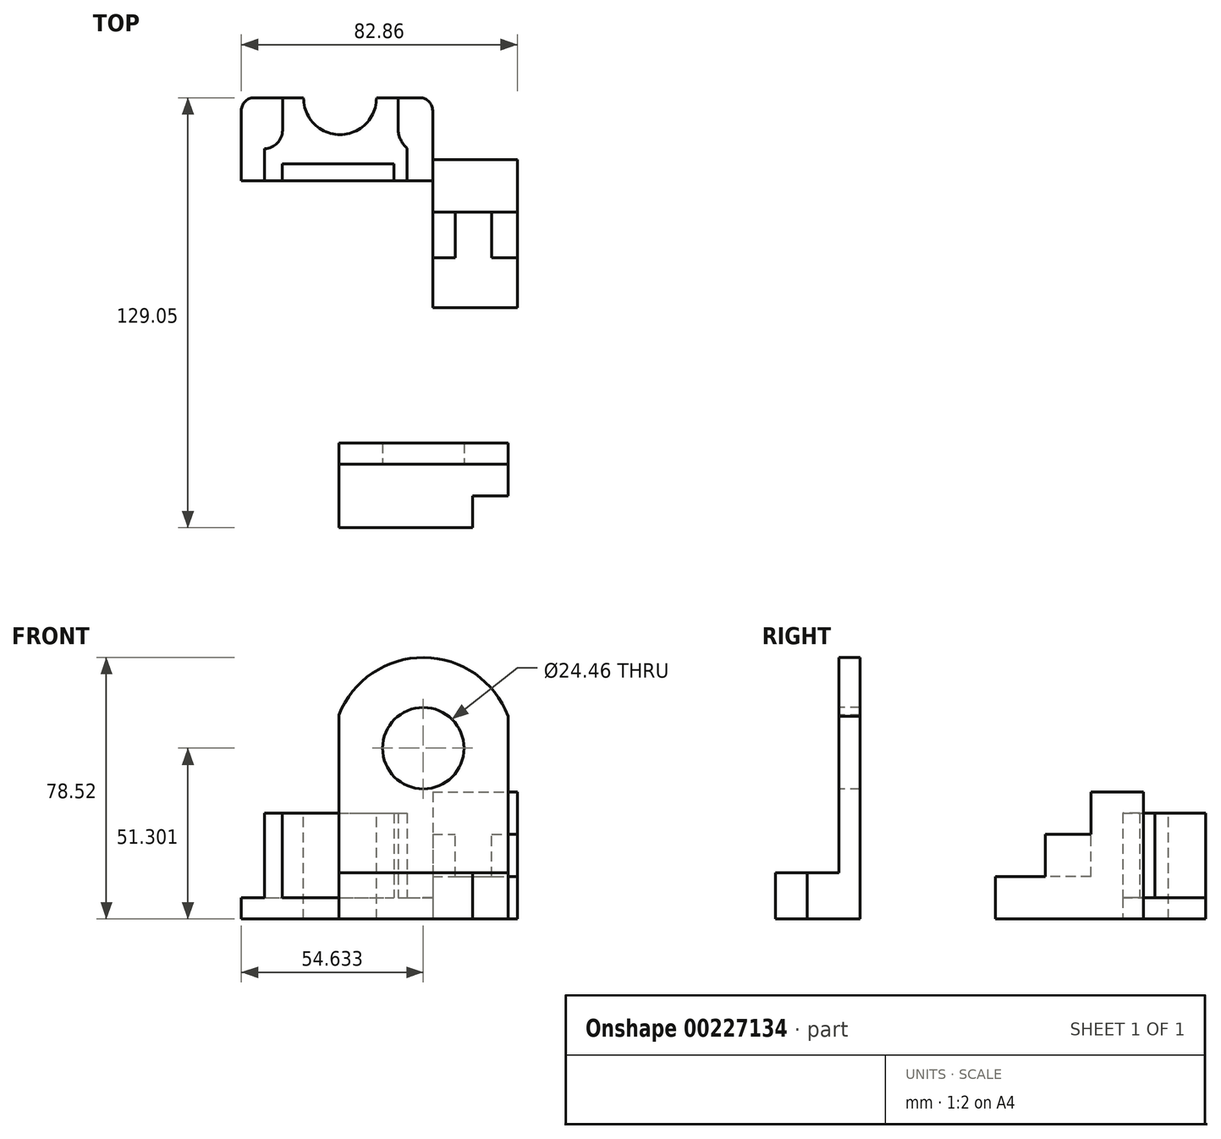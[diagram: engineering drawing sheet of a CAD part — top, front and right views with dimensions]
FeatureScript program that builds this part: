
annotation { "Feature Type Name" : "Feature", "Feature Type Description" : "" }
export const myFeature = defineFeature(function(context is Context, id is Id, definition is map)
    precondition{}
    {
        {
            var Q0;
            Q0=qCreatedBy(makeId("Top.planeOp"),FACE);
            var sketch = newSketch(context, id + "F0", { "sketchPlane" : qUnion([Q0])});
            skLineSegment(sketch, "E0.bottom", {"start": v(0, 0) * mm, "end": v(25.4, 0) * mm});
            skLineSegment(sketch, "E0.top", {"start": v(0, 44.45) * mm, "end": v(25.4, 44.45) * mm});
            skLineSegment(sketch, "E0.left", {"start": v(0, 0) * mm, "end": v(0, 44.45) * mm});
            skLineSegment(sketch, "E0.right", {"start": v(25.4, 0) * mm, "end": v(25.4, 44.45) * mm});
            skSolve(sketch);
        }
        {
            var Q0;
            Q0=makeQuery(id+"F0.imprint","IMPRINT",FACE,{"disambiguationData":[TD([[makeQuery(id+"F0.imprint","IMPRINT",EDGE,{"derivedFrom":sQuery(id+"F0.wireOp",EDGE,"E0.bottom")}),1.0]])]});
            extrude(context, id + "F1", {"entities" : qUnion([Q0]), "depth" : 12.7 * mm});
        }
        {
            var Q0;
            Q0=makeQuery(id+"F1.opExtrude","CAP_FACE",FACE,{"disambiguationData":[OSD([sQuery(id+"F0.wireOp",EDGE,"E0.bottom"),sQuery(id+"F0.wireOp",EDGE,"E0.top"),sQuery(id+"F0.wireOp",EDGE,"E0.left"),sQuery(id+"F0.wireOp",EDGE,"E0.right")])],"isStart":false});
            var sketch = newSketch(context, id + "F2", { "sketchPlane" : qUnion([Q0])});
            skLineSegment(sketch, "E1.bottom", {"start": v(0, 44.45) * mm, "end": v(25.4, 44.45) * mm});
            skLineSegment(sketch, "E1.top", {"start": v(0, 14.99) * mm, "end": v(25.4, 14.99) * mm});
            skLineSegment(sketch, "E1.left", {"start": v(0, 44.45) * mm, "end": v(0, 14.99) * mm});
            skLineSegment(sketch, "E1.right", {"start": v(25.4, 44.45) * mm, "end": v(25.4, 14.99) * mm});
            skSolve(sketch);
        }
        {
            var Q0;
            Q0 = qSketchRegion(id + "F2", true);
            extrude(context, id + "F3", {"entities" : qUnion([Q0]), "operationType" : NewBodyOperationType.ADD, "depth" : 12.7 * mm});
        }
        {
            var Q0;
            Q0=makeQuery(id+"F3.opExtrude","CAP_FACE",FACE,{"disambiguationData":[OSD([sQuery(id+"F2.wireOp",EDGE,"E1.bottom"),sQuery(id+"F2.wireOp",EDGE,"E1.top"),sQuery(id+"F2.wireOp",EDGE,"E1.left"),sQuery(id+"F2.wireOp",EDGE,"E1.right")])],"isStart":false});
            var sketch = newSketch(context, id + "F4", { "sketchPlane" : qUnion([Q0])});
            skLineSegment(sketch, "E2.bottom", {"start": v(6.74, 28.65) * mm, "end": v(17.73, 28.65) * mm});
            skLineSegment(sketch, "E2.top", {"start": v(6.74, 14.99) * mm, "end": v(17.73, 14.99) * mm});
            skLineSegment(sketch, "E2.left", {"start": v(6.74, 28.65) * mm, "end": v(6.74, 14.99) * mm});
            skLineSegment(sketch, "E2.right", {"start": v(17.73, 28.65) * mm, "end": v(17.73, 14.99) * mm});
            skSolve(sketch);
        }
        {
            var Q0;
            Q0 = qSketchRegion(id + "F4", true);
            extrude(context, id + "F5", {"entities" : qUnion([Q0]), "operationType" : NewBodyOperationType.REMOVE, "oppositeDirection" : true, "depth" : 12.7 * mm});
        }
        {
            var Q0;
            Q0=makeQuery(id+"F3.opExtrude","CAP_FACE",FACE,{"disambiguationData":[OSD([sQuery(id+"F2.wireOp",EDGE,"E1.bottom"),sQuery(id+"F2.wireOp",EDGE,"E1.top"),sQuery(id+"F2.wireOp",EDGE,"E1.left"),sQuery(id+"F2.wireOp",EDGE,"E1.right")])],"isStart":false});
            var sketch = newSketch(context, id + "F6", { "sketchPlane" : qUnion([Q0])});
            skLineSegment(sketch, "E3.bottom", {"start": v(0, 44.45) * mm, "end": v(25.4, 44.45) * mm});
            skLineSegment(sketch, "E3.top", {"start": v(0, 28.65) * mm, "end": v(25.4, 28.65) * mm});
            skLineSegment(sketch, "E3.left", {"start": v(0, 44.45) * mm, "end": v(0, 28.65) * mm});
            skLineSegment(sketch, "E3.right", {"start": v(25.4, 44.45) * mm, "end": v(25.4, 28.65) * mm});
            skSolve(sketch);
        }
        {
            var Q0;
            Q0=makeQuery(id+"F6.imprint","IMPRINT",FACE,{"disambiguationData":[TD([[makeQuery(id+"F6.imprint","IMPRINT",EDGE,{"derivedFrom":sQuery(id+"F6.wireOp",EDGE,"E3.bottom")}),-1.0]])]});
            extrude(context, id + "F7", {"entities" : qUnion([Q0]), "operationType" : NewBodyOperationType.ADD, "depth" : 12.7 * mm});
        }
        {
            var Q0;
            Q0=qCreatedBy(makeId("Top.planeOp"),FACE);
            var sketch = newSketch(context, id + "F8", { "sketchPlane" : qUnion([Q0])});
            skLineSegment(sketch, "E4.bottom", {"start": v(-28.17, -66.03) * mm, "end": v(22.63, -66.03) * mm});
            skLineSegment(sketch, "E4.top", {"start": v(-28.17, -40.63) * mm, "end": v(22.63, -40.63) * mm});
            skLineSegment(sketch, "E4.left", {"start": v(-28.17, -66.03) * mm, "end": v(-28.17, -40.63) * mm});
            skLineSegment(sketch, "E4.right", {"start": v(22.63, -66.03) * mm, "end": v(22.63, -40.63) * mm});
            skSolve(sketch);
        }
        {
            var Q0;
            Q0=makeQuery(id+"F8.imprint","IMPRINT",FACE,{"disambiguationData":[TD([[makeQuery(id+"F8.imprint","IMPRINT",EDGE,{"derivedFrom":sQuery(id+"F8.wireOp",EDGE,"E4.bottom")}),1.0]])]});
            extrude(context, id + "F9", {"entities" : qUnion([Q0]), "depth" : 101.6 * mm});
        }
        {
            var Q0;
            Q0=makeQuery(id+"F9.opExtrude","SWEPT_FACE",FACE,{"disambiguationData":[OSD([sQuery(id+"F8.wireOp",EDGE,"E4.bottom")])]});
            var sketch = newSketch(context, id + "F10", { "sketchPlane" : qUnion([Q0])});
            skArc(sketch, "E5", {"start": v(22.63, 60.92) * mm, "mid": v(-2.66, 78.52) * mm, "end": v(-28.17, 61.23) * mm});
            skSolve(sketch);
        }
        {
            var Q0;
            {var subQ0=sQuery(id+"F10.wireOp",EDGE,"E5");Q0=makeQuery(id+"F10.imprint","IMPRINT",FACE,{"disambiguationData":[TD([[makeQuery(id+"F10.imprint","IMPRINT",EDGE,{"derivedFrom":subQ0}),-1.0]])]});}
            extrude(context, id + "F11", {"entities" : qUnion([Q0]), "operationType" : NewBodyOperationType.REMOVE, "oppositeDirection" : true, "depth" : 25.4 * mm});
        }
        {
            var Q0;
            Q0=makeQuery(id+"F9.opExtrude","SWEPT_FACE",FACE,{"disambiguationData":[OSD([sQuery(id+"F8.wireOp",EDGE,"E4.bottom")])]});
            var sketch = newSketch(context, id + "F12", { "sketchPlane" : qUnion([Q0])});
            skCircle(sketch, "E6", {"center": v(-2.83, 51.3) * mm, "radius": 12.23 * mm});
            skSolve(sketch);
        }
        {
            var Q0;
            Q0=makeQuery(id+"F12.imprint","IMPRINT",FACE,{"disambiguationData":[TD([[makeQuery(id+"F12.imprint","IMPRINT",EDGE,{"derivedFrom":sQuery(id+"F12.wireOp",EDGE,"E6")}),1.0]])]});
            extrude(context, id + "F13", {"entities" : qUnion([Q0]), "operationType" : NewBodyOperationType.REMOVE, "oppositeDirection" : true, "depth" : 25.4 * mm});
        }
        {
            var Q0;
            Q0=makeQuery(id+"F9.opExtrude","SWEPT_FACE",FACE,{"disambiguationData":[OSD([sQuery(id+"F8.wireOp",EDGE,"E4.bottom")])]});
            var sketch = newSketch(context, id + "F14", { "sketchPlane" : qUnion([Q0])});
            skLineSegment(sketch, "E7.bottom", {"start": v(-28.17, 13.84) * mm, "end": v(22.63, 13.84) * mm});
            skLineSegment(sketch, "E7.top", {"start": v(-28.17, 0) * mm, "end": v(22.63, 0) * mm});
            skLineSegment(sketch, "E7.left", {"start": v(-28.17, 13.84) * mm, "end": v(-28.17, 0) * mm});
            skLineSegment(sketch, "E7.right", {"start": v(22.63, 13.84) * mm, "end": v(22.63, 0) * mm});
            skSolve(sketch);
        }
        {
            var Q0;
            {var subQ3=sQuery(id+"F14.wireOp",EDGE,"E7.bottom");Q0=makeQuery(id+"F14.imprint","IMPRINT",FACE,{"disambiguationData":[TD([[makeQuery(id+"F14.imprint","IMPRINT",EDGE,{"derivedFrom":subQ3}),1.0]])]});}
            extrude(context, id + "F15", {"entities" : qUnion([Q0]), "operationType" : NewBodyOperationType.REMOVE, "oppositeDirection" : true, "depth" : 19.05 * mm});
        }
        {
            var Q0;
            Q0=makeQuery(id+"F15.boolean.opBoolean","COPY",FACE,{"derivedFrom":makeQuery(id+"F15.opExtrude","SWEPT_FACE",FACE,{"disambiguationData":[OSD([sQuery(id+"F14.wireOp",EDGE,"E7.bottom")])]})});
            var sketch = newSketch(context, id + "F16", { "sketchPlane" : qUnion([Q0])});
            skLineSegment(sketch, "E8.bottom", {"start": v(22.63, -56.5) * mm, "end": v(11.96, -56.5) * mm});
            skLineSegment(sketch, "E8.top", {"start": v(22.63, -66.03) * mm, "end": v(11.96, -66.03) * mm});
            skLineSegment(sketch, "E8.left", {"start": v(22.63, -56.5) * mm, "end": v(22.63, -66.03) * mm});
            skLineSegment(sketch, "E8.right", {"start": v(11.96, -56.5) * mm, "end": v(11.96, -66.03) * mm});
            skSolve(sketch);
        }
        {
            var Q0;
            Q0=makeQuery(id+"F16.imprint","IMPRINT",FACE,{"disambiguationData":[TD([[makeQuery(id+"F16.imprint","IMPRINT",EDGE,{"derivedFrom":sQuery(id+"F16.wireOp",EDGE,"E8.bottom")}),1.0]])]});
            extrude(context, id + "F17", {"entities" : qUnion([Q0]), "operationType" : NewBodyOperationType.REMOVE, "oppositeDirection" : true, "depth" : 25.4 * mm});
        }
        {
            var Q0;
            Q0=qCreatedBy(makeId("Top.planeOp"),FACE);
            var sketch = newSketch(context, id + "F18", { "sketchPlane" : qUnion([Q0])});
            skLineSegment(sketch, "E9.bottom", {"start": v(-53.65, 63.02) * mm, "end": v(-3.81, 63.02) * mm});
            skLineSegment(sketch, "E9.top", {"start": v(-57.46, 38.14) * mm, "end": v(0, 38.14) * mm});
            skLineSegment(sketch, "E9.left", {"start": v(-57.46, 59.21) * mm, "end": v(-57.46, 38.14) * mm});
            skLineSegment(sketch, "E9.right", {"start": v(0, 59.21) * mm, "end": v(0, 38.14) * mm});
            skPoint(sketch, "E10.visualSharp", {"position": v(-57.46, 63.02) * mm});
            skArc(sketch, "E10.filletArc", {"start": v(-53.65, 63.02) * mm, "mid": v(-56.35, 61.9) * mm, "end": v(-57.46, 59.21) * mm});
            skPoint(sketch, "E11.visualSharp", {"position": v(0, 63.02) * mm});
            skArc(sketch, "E11.filletArc", {"start": v(0, 59.21) * mm, "mid": v(-1.12, 61.9) * mm, "end": v(-3.81, 63.02) * mm});
            skSolve(sketch);
        }
        {
            var Q0;
            Q0=makeQuery(id+"F18.imprint","IMPRINT",FACE,{"disambiguationData":[TD([[makeQuery(id+"F18.imprint","IMPRINT",EDGE,{"derivedFrom":sQuery(id+"F18.wireOp",EDGE,"E9.bottom")}),-1.0]])]});
            extrude(context, id + "F19", {"entities" : qUnion([Q0]), "operationType" : NewBodyOperationType.ADD, "depth" : 6.35 * mm});
        }
        {
            var Q0;
            Q0=makeQuery(id+"F19.opExtrude","CAP_FACE",FACE,{"disambiguationData":[OSD([sQuery(id+"F18.wireOp",EDGE,"E9.bottom"),sQuery(id+"F18.wireOp",EDGE,"E9.top"),sQuery(id+"F18.wireOp",EDGE,"E9.left"),sQuery(id+"F18.wireOp",EDGE,"E9.right"),sQuery(id+"F18.wireOp",EDGE,"E10.filletArc"),sQuery(id+"F18.wireOp",EDGE,"E11.filletArc")])],"isStart":false});
            var sketch = newSketch(context, id + "F20", { "sketchPlane" : qUnion([Q0])});
            skArc(sketch, "E12", {"start": v(-38.77, 63.02) * mm, "mid": v(-27.84, 51.95) * mm, "end": v(-16.9, 63.02) * mm});
            skSolve(sketch);
        }
        {
            var Q0;
            {var subQ0=sQuery(id+"F20.wireOp",EDGE,"E12");Q0=makeQuery(id+"F20.imprint","IMPRINT",FACE,{"disambiguationData":[TD([[makeQuery(id+"F20.imprint","IMPRINT",EDGE,{"derivedFrom":subQ0}),1.0]])]});}
            extrude(context, id + "F21", {"entities" : qUnion([Q0]), "operationType" : NewBodyOperationType.REMOVE, "oppositeDirection" : true, "depth" : 25.4 * mm});
        }
        {
            var Q0;
            Q0=makeQuery(id+"F19.opExtrude","CAP_FACE",FACE,{"disambiguationData":[OSD([sQuery(id+"F18.wireOp",EDGE,"E9.bottom"),sQuery(id+"F18.wireOp",EDGE,"E9.top"),sQuery(id+"F18.wireOp",EDGE,"E9.left"),sQuery(id+"F18.wireOp",EDGE,"E9.right"),sQuery(id+"F18.wireOp",EDGE,"E10.filletArc"),sQuery(id+"F18.wireOp",EDGE,"E11.filletArc")])],"isStart":false});
            var sketch = newSketch(context, id + "F22", { "sketchPlane" : qUnion([Q0])});
            skLineSegment(sketch, "E13.bottom", {"start": v(-45.23, 43.23) * mm, "end": v(-11.69, 43.23) * mm});
            skLineSegment(sketch, "E13.top", {"start": v(-45.23, 38.14) * mm, "end": v(-11.69, 38.14) * mm});
            skLineSegment(sketch, "E13.left", {"start": v(-45.23, 43.23) * mm, "end": v(-45.23, 38.14) * mm});
            skLineSegment(sketch, "E13.right", {"start": v(-11.69, 43.23) * mm, "end": v(-11.69, 38.14) * mm});
            skLineSegment(sketch, "E14", {"start": v(-50.45, 38.14) * mm, "end": v(-50.45, 47.76) * mm});
            skLineSegment(sketch, "E15", {"start": v(-7.7, 38.14) * mm, "end": v(-7.7, 47.9) * mm});
            skLineSegment(sketch, "E16", {"start": v(-45.1, 63.02) * mm, "end": v(-45.1, 53.26) * mm});
            skLineSegment(sketch, "E17", {"start": v(-10.36, 63.02) * mm, "end": v(-10.36, 53.68) * mm});
            skArc(sketch, "E18", {"start": v(-50.45, 47.76) * mm, "mid": v(-46.65, 49.42) * mm, "end": v(-45.1, 53.26) * mm});
            skArc(sketch, "E19", {"start": v(-10.36, 53.68) * mm, "mid": v(-9.66, 50.5) * mm, "end": v(-7.7, 47.9) * mm});
            skSolve(sketch);
        }
        {
            var Q0;
            Q0=makeQuery(id+"F22.imprint","IMPRINT",FACE,{"disambiguationData":[TD([[makeQuery(id+"F22.imprint","IMPRINT",EDGE,{"derivedFrom":sQuery(id+"F22.wireOp",EDGE,"E13.bottom")}),1.0]])]});
            extrude(context, id + "F23", {"entities" : qUnion([Q0]), "operationType" : NewBodyOperationType.ADD, "depth" : 25.4 * mm});
        }
    });
